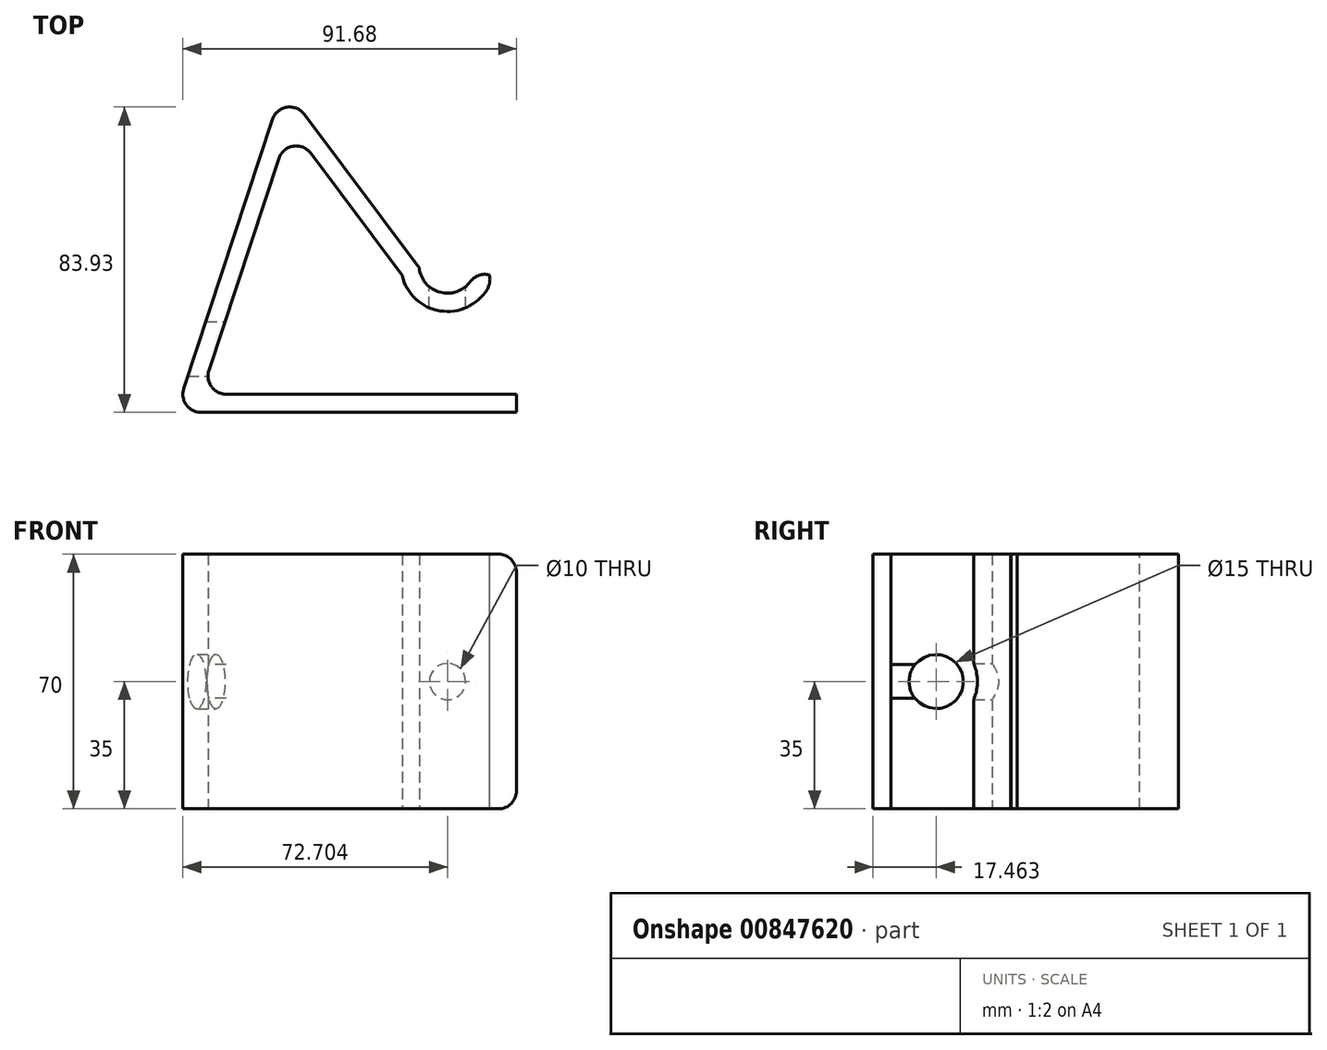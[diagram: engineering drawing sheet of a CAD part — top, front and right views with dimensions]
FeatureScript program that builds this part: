
annotation { "Feature Type Name" : "Feature", "Feature Type Description" : "" }
export const myFeature = defineFeature(function(context is Context, id is Id, definition is map)
    precondition{}
    {
        {
            var Q0;
            Q0=qCreatedBy(makeId("Top.planeOp"),FACE);
            var sketch = newSketch(context, id + "F0", { "sketchPlane" : qUnion([Q0])});
            skLineSegment(sketch, "E0", {"start": v(-46.6, -35.55) * mm, "end": v(40.08, -35.55) * mm});
            skLineSegment(sketch, "E1", {"start": v(-46.6, -35.55) * mm, "end": v(-22.24, 38.38) * mm});
            skLineSegment(sketch, "E2", {"start": v(-22.24, 38.38) * mm, "end": v(8.64, -2.97) * mm});
            skArc(sketch, "E3", {"start": v(8.64, -2.97) * mm, "mid": v(21.1, -12.81) * mm, "end": v(33.57, -2.97) * mm});
            skArc(sketch, "E4.0", {"start": v(13.34, -0.92) * mm, "mid": v(20.65, -7.8) * mm, "end": v(28.7, -1.81) * mm});
            skLineSegment(sketch, "E4.1", {"start": v(-23.98, 49.07) * mm, "end": v(13.34, -0.92) * mm});
            skLineSegment(sketch, "E4.2", {"start": v(-53.51, -40.55) * mm, "end": v(-23.98, 49.07) * mm});
            skLineSegment(sketch, "E4.3", {"start": v(-53.51, -40.55) * mm, "end": v(40.08, -40.55) * mm});
            skLineSegment(sketch, "E5", {"start": v(28.7, -1.81) * mm, "end": v(33.57, -2.97) * mm});
            skLineSegment(sketch, "E6", {"start": v(40.08, -35.55) * mm, "end": v(40.08, -40.55) * mm});
            skSolve(sketch);
        }
        {
            var Q0;
            Q0=makeQuery(id+"F0.imprint","IMPRINT",FACE,{"disambiguationData":[TD([[makeQuery(id+"F0.imprint","IMPRINT",EDGE,{"derivedFrom":sQuery(id+"F0.wireOp",EDGE,"E0")}),-1.0]])]});
            var Q1;
            Q1=sQuery(id+"F0.wireOp",EDGE,"E0");
            var Q2;
            Q2=sQuery(id+"F0.wireOp",EDGE,"E1");
            var Q3;
            Q3=sQuery(id+"F0.wireOp",EDGE,"E3");
            var Q4;
            Q4=sQuery(id+"F0.wireOp",EDGE,"E4.0");
            var Q5;
            Q5=sQuery(id+"F0.wireOp",EDGE,"E4.1");
            var Q6;
            Q6=sQuery(id+"F0.wireOp",EDGE,"E4.2");
            var Q7;
            Q7=sQuery(id+"F0.wireOp",EDGE,"E4.3");
            extrude(context, id + "F1", {"entities" : qUnion([Q0]), "surfaceEntities" : qUnion([Q1, Q2, Q3, Q4, Q5, Q6, Q7]), "depth" : 70 * mm, "offsetDistance" : 25 * mm});
        }
        {
            var Q0;
            Q0=qCreatedBy(makeId("Right.planeOp"),FACE);
            var sketch = newSketch(context, id + "F2", { "sketchPlane" : qUnion([Q0])});
            skCircle(sketch, "E7", {"center": v(-23.09, 35) * mm, "radius": 7.5 * mm});
            skSolve(sketch);
        }
        {
            var Q0;
            Q0=makeQuery(id+"F2.imprint","IMPRINT",FACE,{"disambiguationData":[TD([[makeQuery(id+"F2.imprint","IMPRINT",EDGE,{"derivedFrom":sQuery(id+"F2.wireOp",EDGE,"E7")}),1.0]])]});
            extrude(context, id + "F3", {"entities" : qUnion([Q0]), "operationType" : NewBodyOperationType.REMOVE, "endBound" : BoundingType.THROUGH_ALL, "oppositeDirection" : true, "depth" : 25 * mm, "offsetDistance" : 25 * mm});
        }
        {
            var Q0;
            Q0=qCreatedBy(makeId("Front.planeOp"),FACE);
            var sketch = newSketch(context, id + "F4", { "sketchPlane" : qUnion([Q0])});
            skCircle(sketch, "E8", {"center": v(21.1, 35) * mm, "radius": 5 * mm});
            skSolve(sketch);
        }
        {
            var Q0;
            Q0=makeQuery(id+"F4.imprint","IMPRINT",FACE,{"disambiguationData":[TD([[makeQuery(id+"F4.imprint","IMPRINT",EDGE,{"derivedFrom":sQuery(id+"F4.wireOp",EDGE,"E8")}),1.0]])]});
            extrude(context, id + "F5", {"entities" : qUnion([Q0]), "operationType" : NewBodyOperationType.REMOVE, "depth" : 25 * mm, "offsetDistance" : 25 * mm});
        }
        {
            var Q0;
            Q0=makeQuery(id+"F1.opExtrude","SWEPT_EDGE",EDGE,{"disambiguationData":[OSD([sQuery(id+"F0.wireOp",EDGE,"E4.1"),sQuery(id+"F0.wireOp",EDGE,"E4.2")])]});
            var Q1;
            Q1=makeQuery(id+"F1.opExtrude","SWEPT_EDGE",EDGE,{"disambiguationData":[OSD([sQuery(id+"F0.wireOp",EDGE,"E4.0"),sQuery(id+"F0.wireOp",EDGE,"E5")])]});
            var Q2;
            Q2=makeQuery(id+"F1.opExtrude","SWEPT_EDGE",EDGE,{"disambiguationData":[OSD([sQuery(id+"F0.wireOp",EDGE,"E0"),sQuery(id+"F0.wireOp",EDGE,"E1")])]});
            fillet(context, id + "F6", {"entities" : qUnion([Q0, Q1, Q2]), "radius" : 5 * mm, "tangentPropagation" : true, "allowEdgeOverflow" : false});
        }
        {
            var Q0;
            Q0=makeQuery(id+"F1.opExtrude","SWEPT_EDGE",EDGE,{"disambiguationData":[OSD([sQuery(id+"F0.wireOp",EDGE,"E3"),sQuery(id+"F0.wireOp",EDGE,"E5")])]});
            fillet(context, id + "F7", {"entities" : qUnion([Q0]), "radius" : 5 * mm, "tangentPropagation" : true, "allowEdgeOverflow" : false});
        }
        {
            var Q0;
            Q0=makeQuery(id+"F1.opExtrude","CAP_EDGE",EDGE,{"disambiguationData":[OSD([sQuery(id+"F0.wireOp",EDGE,"E6")])],"isStart":false});
            var Q1;
            Q1=makeQuery(id+"F1.opExtrude","CAP_EDGE",EDGE,{"disambiguationData":[OSD([sQuery(id+"F0.wireOp",EDGE,"E6")])],"isStart":true});
            fillet(context, id + "F8", {"entities" : qUnion([Q0, Q1]), "radius" : 5 * mm, "tangentPropagation" : true, "allowEdgeOverflow" : false});
        }
        {
            var Q0;
            Q0=makeQuery(id+"F1.opExtrude","SWEPT_EDGE",EDGE,{"disambiguationData":[OSD([sQuery(id+"F0.wireOp",EDGE,"E4.2"),sQuery(id+"F0.wireOp",EDGE,"E4.3")])]});
            fillet(context, id + "F9", {"entities" : qUnion([Q0]), "radius" : 5 * mm, "tangentPropagation" : true, "allowEdgeOverflow" : false});
        }
        {
            var Q0;
            Q0=makeQuery(id+"F1.opExtrude","SWEPT_EDGE",EDGE,{"disambiguationData":[OSD([sQuery(id+"F0.wireOp",EDGE,"E1"),sQuery(id+"F0.wireOp",EDGE,"E2")])]});
            fillet(context, id + "F10", {"entities" : qUnion([Q0]), "radius" : 5 * mm, "tangentPropagation" : true, "allowEdgeOverflow" : false});
        }
    });
